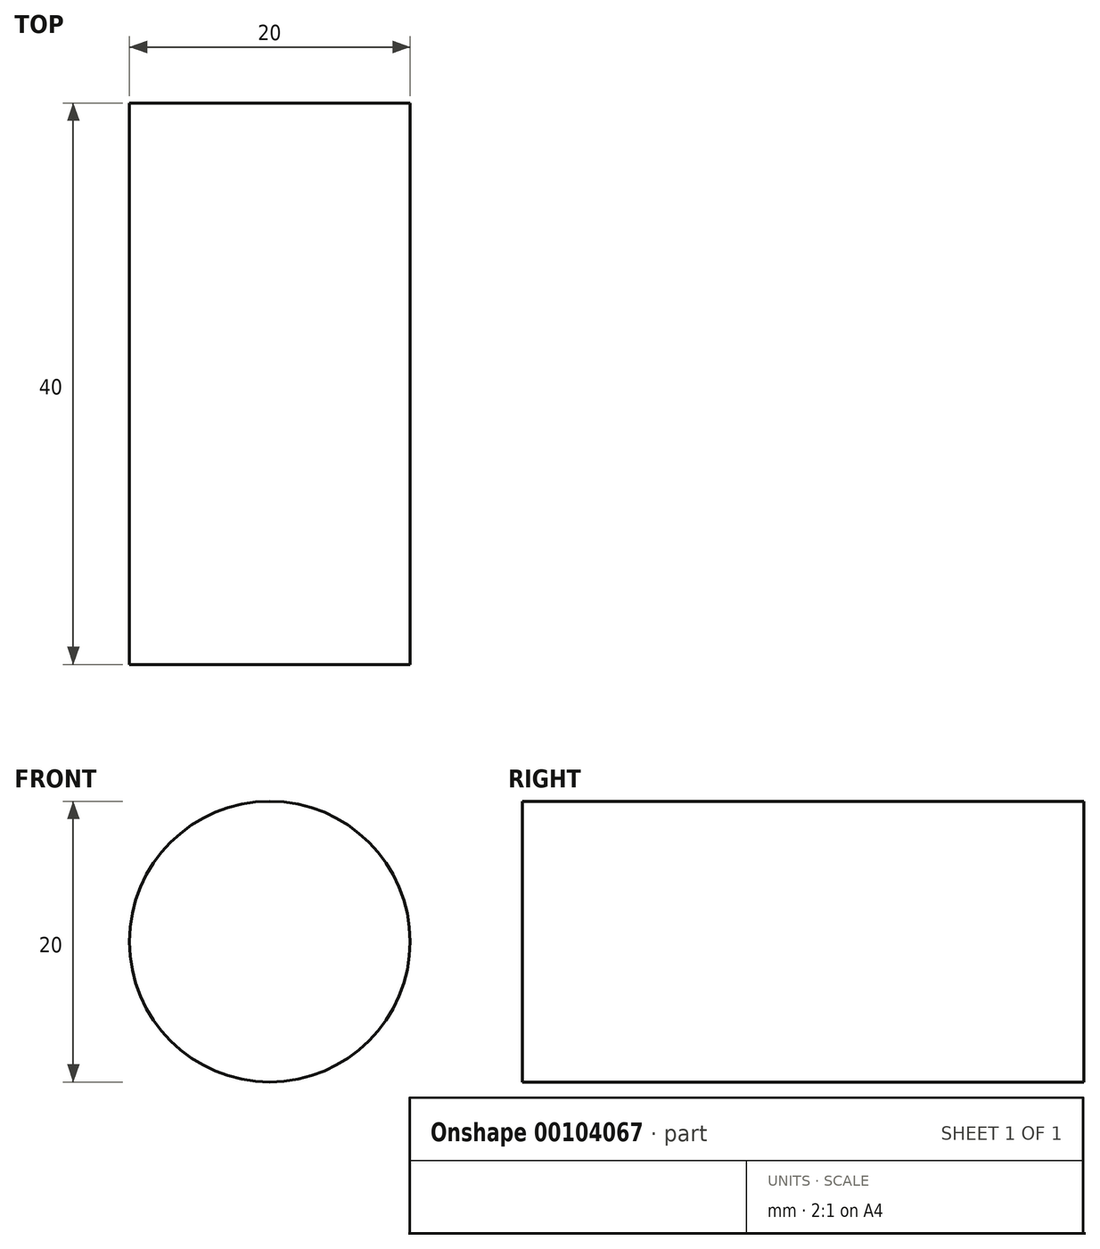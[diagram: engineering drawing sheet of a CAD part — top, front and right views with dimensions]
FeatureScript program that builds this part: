
annotation { "Feature Type Name" : "Feature", "Feature Type Description" : "" }
export const myFeature = defineFeature(function(context is Context, id is Id, definition is map)
    precondition{}
    {
        {
            var Q0;
            Q0=qCreatedBy(makeId("Front.planeOp"),FACE);
            var sketch = newSketch(context, id + "F0", { "sketchPlane" : qUnion([Q0])});
            skCircle(sketch, "E0", {"center": v(-9.18, 6.65) * mm, "radius": 10 * mm});
            skSolve(sketch);
        }
        {
            var Q0;
            Q0=makeQuery(id+"F0.imprint","IMPRINT",FACE,{"disambiguationData":[TD([[makeQuery(id+"F0.imprint","IMPRINT",EDGE,{"derivedFrom":sQuery(id+"F0.wireOp",EDGE,"E0")}),1.0]])]});
            extrude(context, id + "F1", {"entities" : qUnion([Q0]), "depth" : 40 * mm});
        }
    });
